# Revit family: ITK by ZPAS__Органайзер кабельный металлический с крышкой 19
name_source: partatom
category: Обобщенные модели
units: mm (PartAtom-declared; Revit-internal decimal feet)

## family parameters
Всегда вертикально = Да
Может служить основой для арматурных стержней = Нет
На основе рабочей плоскости = Нет
Общий = Нет
При загрузке вырезать с полостями = Нет
Размер круглого соединителя = Использовать диаметр
Тип детали = Нормальный
Точка расчета площади = Нет

## types (1)
- ZP-CO05-1U-24-M-C
    ADSK_URL страницы изделия = https://www.itk-group.ru
    ADSK_Версия Revit = 2019
    ADSK_Версия семейства = 1.0
    ADSK_Группирование = I. ЩИТЫ И ПУЛЬТЫ
    ADSK_Единица измерения = шт
    ADSK_Завод-изготовитель = IEK
    ADSK_Код изделия = ZP-CO05-1U-24-M-C
    ADSK_Марка = by ZPAS
    ADSK_Масса = 0.52
    ADSK_Материал наименование = Листовая сталь
    ADSK_Наименование = ITK by ZPAS Органайзер мет. с крышкой 19" 1U 24 сл. черн.
    IEK_URL = https://www.itk-group.ru
    IEK_Описание = На тыльной стороне органайзера имеются отверстия для ввода кабелей.
Cъемная лицевая крышка.
Монтажная высота 1U и 2U.
    IEK_Цена за единицу = 754.02
    KSI_CMa_Строительные материалы = 10.03.02.06
    KSI_CPr_Строительные изделия = 61.1.04.08
    URL = https://www.iek.ru
    Высота = 45 мм
    Глубина = 45 мм
    Изготовитель = ITK
    Материал = Окраска - RAL 9005
    Ширина = 482 мм
